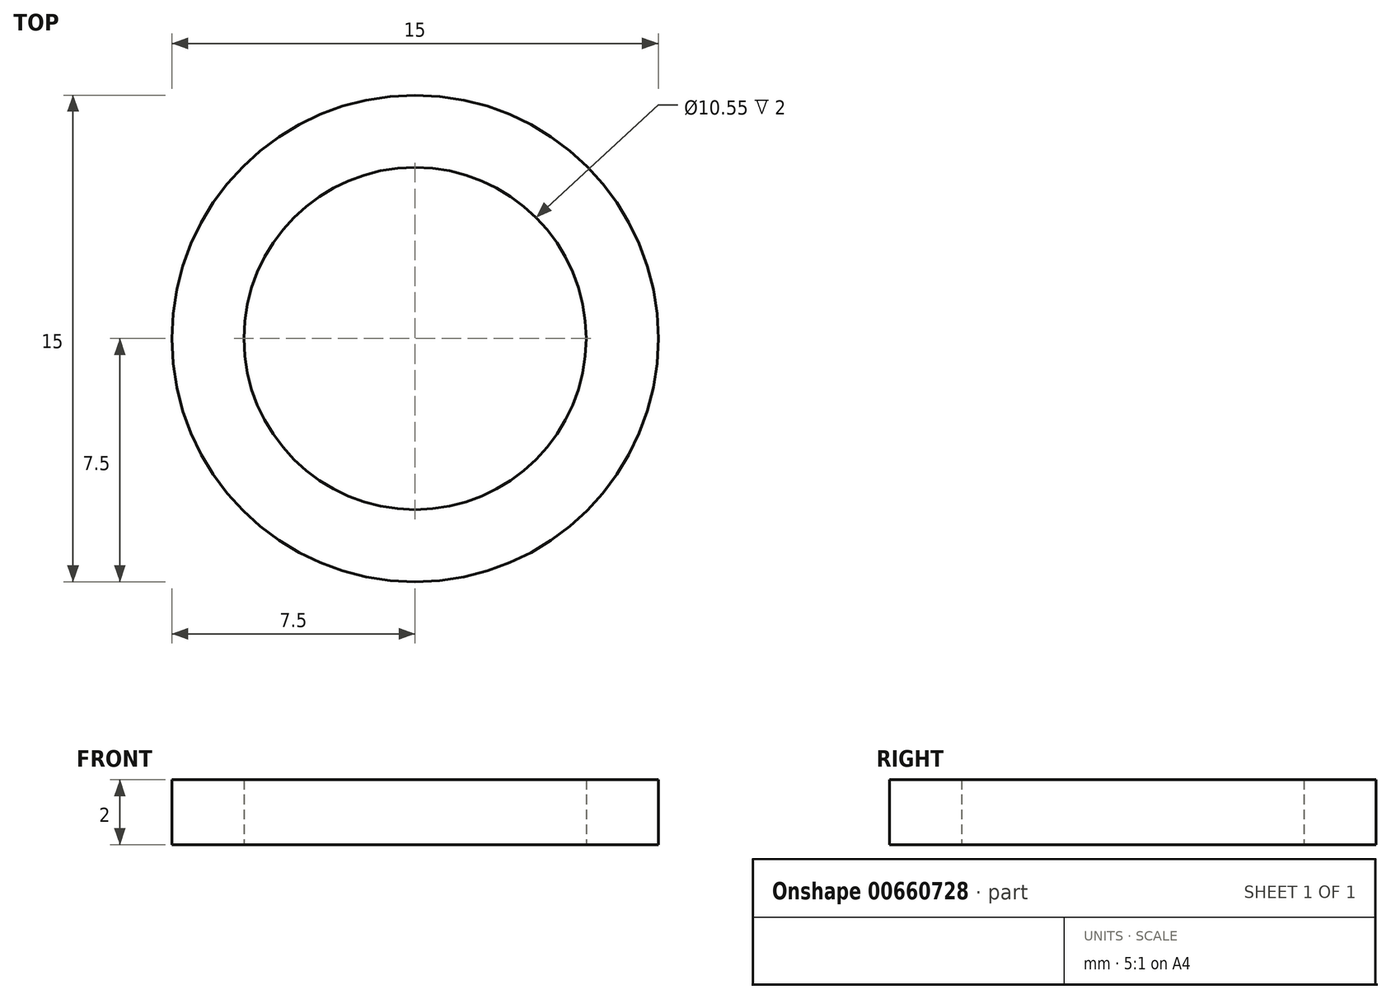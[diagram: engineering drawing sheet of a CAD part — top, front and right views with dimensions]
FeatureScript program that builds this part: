
annotation { "Feature Type Name" : "Feature", "Feature Type Description" : "" }
export const myFeature = defineFeature(function(context is Context, id is Id, definition is map)
    precondition{}
    {
        {
            var Q0;
            Q0=qCreatedBy(makeId("Top.planeOp"),FACE);
            var sketch = newSketch(context, id + "F0", { "sketchPlane" : qUnion([Q0])});
            skCircle(sketch, "E0", {"center": v(0, 0) * mm, "radius": 7.5 * mm});
            skCircle(sketch, "E1", {"center": v(0, 0) * mm, "radius": 5.28 * mm});
            skSolve(sketch);
        }
        {
            var Q0;
            Q0 = qSketchRegion(id + "F0", true);
            extrude(context, id + "F1", {"entities" : qUnion([Q0]), "depth" : 2 * mm, "offsetDistance" : 25 * mm});
        }
    });
